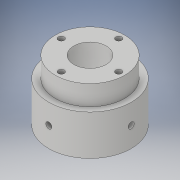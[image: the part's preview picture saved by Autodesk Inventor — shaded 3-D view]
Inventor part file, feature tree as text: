
AUTODESK INVENTOR PART (.ipt)
format: ipt  version: 2019 (Build 230136000, 136)  size: 179,712 bytes
history: native  units: mm
features: sketch x9, extrude x8, pattern_circular x2, plane x1, projected_geometry x1
ambient origin geometry x8: Origin, YZ Plane, XZ Plane, XY Plane, X Axis, Y Axis, Z Axis, Center Point
bodies: Solid1 (feature_tree)
feature tree (21):
  extrude  "Extrusion1"  Depth=30.0mm
  extrude  "Extrusion2"  Depth=5.0mm TaperAngle=0.0deg
  sketch  "Sketch4"  dims[d19=40.0mm d20=360.0deg d22=1.5mm]
  extrude  "Extrusion5"  Depth=1.5mm
  pattern_circular  "Circular Pattern2"  [2 undecoded]
  extrude  "Extrusion6"  Depth=50.0mm TaperAngle=0.0deg
  extrude  "Extrusion7"  Depth=10.1mm TaperAngle=360.0deg
  extrude  "Extrusion8"  Depth=10.1mm TaperAngle=0.0deg
  sketch  "Sketch8"  dims[d28=10.0mm]
  plane  "Work Plane1"
  extrude  "Extrusion9"  [1 undecoded]
  pattern_circular  "Circular Pattern3"  [2 undecoded]
  extrude  "Extrusion10"  [1 undecoded]
  sketch  "Sketch1"  dims[d1=30.0mm d2=0.0mm d3=16.1mm]
  sketch  "Sketch2"  dims[d4=13.0mm d5=0.0mm d17=5.0mm d18=0.0mm]
  sketch  "Sketch5"  dims[d23=10.0mm d24=0.0mm]
  sketch  "Sketch6"  dims[d25=10.0mm d26=0.0mm]
  sketch  "Sketch7"  dims[d27=6.0mm]
  projected_geometry  "Projected Loop1"
  sketch  "Sketch9"  dims[d29=14.0mm d30=0.0mm]
  sketch  "Sketch10"  dims[d31=17.5mm d32=3.0mm d33=50.0mm d34=50.0mm d35=0.0mm d36=0.0mm d37=40.0mm d38=360.0deg d46=10.1mm d47=0.0mm]
note: 6 required parameter values undecoded (feature->parameter linkage not recoverable at this tier; creation-order binding heuristic only, values carry confidence <= 0.55)
